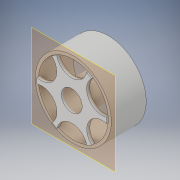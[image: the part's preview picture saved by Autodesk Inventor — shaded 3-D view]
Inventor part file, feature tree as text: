
AUTODESK INVENTOR PART (.ipt)
format: ipt  version: 2017 (Build 210142000, 142)  size: 187,392 bytes
history: native  units: in
note: dims shown in document units (in); Inventor stores cm internally (conversion verified against a paired STEP export)
features: extrude x3, sketch x3, projected_geometry x2, plane x1, pattern_circular x1
ambient origin geometry x8: Origin, YZ Plane, XZ Plane, XY Plane, X Axis, Y Axis, Z Axis, Center Point
bodies: Solid1 (feature_tree)
feature tree (10):
  extrude  "Extrusion1"  Depth=0.05in
  plane  "Work Plane1"
  extrude  "Extrusion2"  Depth=0.05in
  extrude  "Extrusion3"  TaperAngle=0.0deg  [1 undecoded]
  pattern_circular  "Circular Pattern1"  [2 undecoded]
  sketch  "Sketch1"  dims[d0=0.44in d1=0.05in]
  sketch  "Sketch2"  dims[d2=0.35in d3=0.05in]
  projected_geometry  "Projected Loop1"
  projected_geometry  "Projected Loop2"
  sketch  "Sketch3"  dims[d4=0.57in d5=0.0in d6=0.0in d7=0.05in d8=0.0in d9=0.5in d10=0.05in d11=0.0in d12=2.3622in d13=360.0deg]
note: 3 required parameter values undecoded (feature->parameter linkage not recoverable at this tier; creation-order binding heuristic only, values carry confidence <= 0.55)
